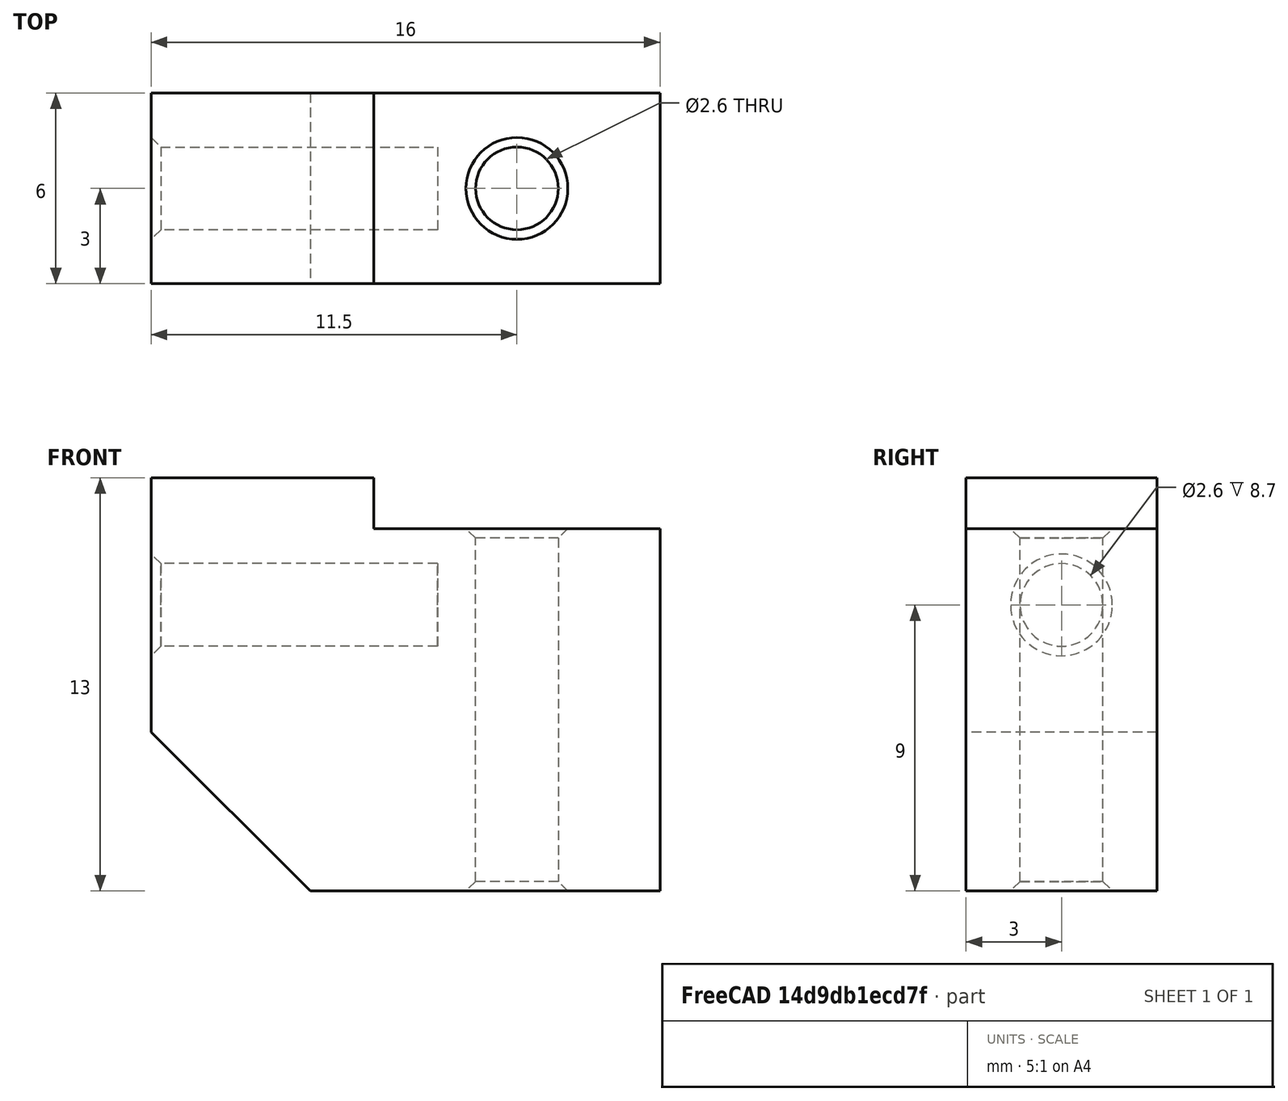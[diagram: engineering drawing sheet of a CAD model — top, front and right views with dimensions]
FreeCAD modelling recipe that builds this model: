
FCSTD DOCUMENT  (FreeCAD 0.21R33675 (Git))
Label: PMB-1
License: All rights reserved
LicenseURL: http://en.wikipedia.org/wiki/All_rights_reserved
objects: TechDraw::DrawViewDimension×9, Sketcher::SketchObject×3, TechDraw::DrawProjGroupItem×3, PartDesign::Pocket×2, PartDesign::Pad×1, PartDesign::Chamfer×1, PartDesign::Body×1, TechDraw::DrawSVGTemplate×1, TechDraw::DrawProjGroup×1, TechDraw::DrawPage×1, Part::Feature×1
note: 27 computed .brp shape members not serialized (recipe doc carries the construction recipe); baked Part::Feature solids carry a one-line shape summary decoded from their .brp

FEATURE [Sketcher::SketchObject] Sketch
  FullyConstrained = true
  MapMode = 5
  Placement = pos=(0,0,0) rot=(1,0,0;1.5708rad)
  Support = -> [XZ_Plane]
  sketch-geometry (7):
    g0: LineSegment StartX=-2e-15 StartY=-2.082e-13 StartZ=0 EndX=7 EndY=-2.082e-13 EndZ=0
    g1: LineSegment StartX=7 StartY=-2.082e-13 StartZ=0 EndX=7 EndY=-1.6 EndZ=0
    g2: LineSegment StartX=7 StartY=-1.6 StartZ=0 EndX=16 EndY=-1.6 EndZ=0
    g3: LineSegment StartX=16 StartY=-1.6 StartZ=0 EndX=16 EndY=-13 EndZ=0
    g4: LineSegment StartX=16 StartY=-13 StartZ=0 EndX=5 EndY=-13 EndZ=0
    g5: LineSegment StartX=5 StartY=-13 StartZ=0 EndX=-2e-15 EndY=-8 EndZ=0
    g6: LineSegment StartX=-2e-15 StartY=-8 StartZ=0 EndX=-2e-15 EndY=-2.078e-13 EndZ=0
  constraints (20):
    c: Horizontal(g0)
    c: Coincident(g0,g1)
    c: Vertical(g1)
    c: Coincident(g1,g2)
    c: Horizontal(g2)
    c: Coincident(g2,g3)
    c: Vertical(g3)
    c: Coincident(g3,g4)
    c: Horizontal(g4)
    c: Coincident(g4,g5)
    c: Coincident(g5,g6)
    c: Coincident(g6,g0)
    c: Coincident(g0,g-1)
    c: Vertical(g6)
    c: DistanceX(g2) = 16
    c: DistanceX(g1,g2) = 9
    c: DistanceY(g1,g1) = 1.6
    c: DistanceY(g4,g0) = 13
    c: Angle(g4,g5) = 2.35619
    c: DistanceX(g5,g4) = 5
FEATURE [PartDesign::Pad] Pad
  Direction = (0,-1,2e-16)
  Length = 6
  Length2 = 10
  Midplane = true
  Placement = pos=(0,0,0) rot=(1,0,0;1.5708rad)
  Profile = -> Sketch
  ReferenceAxis = -> Sketch [N_Axis]
  Type = 0
FEATURE [Sketcher::SketchObject] Sketch001
  FullyConstrained = true
  MapMode = 5
  Support = -> [XY_Plane]
  sketch-geometry (1):
    g0: Circle CenterX=11.5 CenterY=0 CenterZ=0 NormalX=0 NormalY=0 NormalZ=1 AngleXU=0 Radius=1.3
  constraints (3):
    c: PointOnObject(g0,g-1)
    c: DistanceX(g-1,g0) = 11.5
    c: Diameter(g0) = 2.6
FEATURE [PartDesign::Pocket] Pocket
  BaseFeature = -> Pad
  Direction = (0,0,-1)
  Length = 5
  Length2 = 5
  Placement = pos=(0,0,0) rot=(1,0,0;1.5708rad)
  Profile = -> Sketch001
  ReferenceAxis = -> Sketch001 [N_Axis]
  Type = 1
FEATURE [Sketcher::SketchObject] Sketch002
  FullyConstrained = true
  MapMode = 5
  Placement = pos=(0,0,0) rot=(0.57735,0.57735,0.57735;2.0944rad)
  Support = -> [YZ_Plane]
  sketch-geometry (1):
    g0: Circle CenterX=5.7234e-12 CenterY=-4 CenterZ=0 NormalX=0 NormalY=0 NormalZ=1 AngleXU=0 Radius=1.3
  constraints (3):
    c: Vertical(g0,g-1)
    c: DistanceY(g0,g-1) = 4
    c: Diameter(g0) = 2.6
FEATURE [PartDesign::Pocket] Pocket001
  BaseFeature = -> Pocket
  Direction = (-1,2e-16,-3e-16)
  Length = 9
  Length2 = 5
  Placement = pos=(0,0,0) rot=(1,0,0;1.5708rad)
  Profile = -> Sketch002
  ReferenceAxis = -> Sketch002 [N_Axis]
  Reversed = true
  Type = 0
FEATURE [PartDesign::Chamfer] Chamfer
  Angle = 45
  Base = -> Pocket001 [Edge24,Edge26,Edge8]
  BaseFeature = -> Pocket001
  ChamferType = 0
  FlipDirection = false
  Placement = pos=(0,0,0) rot=(1,0,0;1.5708rad)
  Size = 0.3
  Size2 = 1
  SupportTransform = false
  UseAllEdges = false
FEATURE [PartDesign::Body] Body
  Group = -> [Sketch,Pad,Sketch001,Pocket,Sketch002,Pocket001,Chamfer]
  Origin = -> Origin
  Tip = -> Chamfer
FEATURE [TechDraw::DrawSVGTemplate] Template
  EditableTexts = Designed_by_Name=Designed by Name; Drawing_number=Drawing number; FC-Date=Date; FC-SC=Scale; FC-SH=Sheet; FC-Title=Title; Subtitle=Subtitle; Weight=Weight
  Height = 210
  Orientation = 1
  Template = /Applications/FreeCAD-0.21-arm64.app/Contents/Resources/share/Mod/TechDraw/Templates/A4_LandscapeTD.svg
  Width = 297
FEATURE [TechDraw::DrawProjGroupItem] ProjItem  label="Front"
  CoarseView = false
  Direction = (0,-1,0)
  Focus = 100
  HardHidden = false
  IsoCount = 0
  IsoHidden = false
  IsoVisible = true
  LockPosition = true
  Perspective = false
  Rotation = 0
  RotationVector = (1,0,0)
  Scale = 3
  ScaleType = 2
  ScrubCount = 0
  SeamHidden = false
  SeamVisible = false
  SmoothHidden = false
  SmoothVisible = true
  Source = -> [Chamfer]
  Type = 0
  X = 0
  XDirection = (1,0,0)
  Y = 0
FEATURE [TechDraw::DrawProjGroupItem] ProjItem001  label="Top"
  CoarseView = false
  Direction = (0,0,1)
  Focus = 100
  HardHidden = false
  IsoCount = 0
  IsoHidden = false
  IsoVisible = false
  LockPosition = false
  Perspective = false
  Rotation = 0
  RotationVector = (1,0,0)
  ScaleType = 2
  ScrubCount = 0
  SeamHidden = false
  SeamVisible = false
  SmoothHidden = false
  SmoothVisible = true
  Source = -> [Chamfer]
  Type = 4
  X = 0
  XDirection = (1,0,0)
  Y = 53.5
FEATURE [TechDraw::DrawViewDimension] Dimension002
  AngleOverride = false
  Arbitrary = false
  ArbitraryTolerances = false
  EqualTolerance = true
  ExtensionAngle = 0
  FormatSpec = %.2w
  FormatSpecOverTolerance = %+.2w
  FormatSpecUnderTolerance = %+.2w
  Inverted = false
  LineAngle = 0
  LockPosition = false
  MeasureType = 1
  OverTolerance = 0
  References2D = -> [ProjItem001]
  Rotation = 0
  ScaleType = 0
  TheoreticalExact = false
  Type = 1
  UnderTolerance = 0
  X = 8.70547
  Y = -13.6781
FEATURE [TechDraw::DrawViewDimension] Dimension003
  AngleOverride = false
  Arbitrary = false
  ArbitraryTolerances = false
  EqualTolerance = true
  ExtensionAngle = 0
  FormatSpec = ⌀%.2w
  FormatSpecOverTolerance = %+.2w
  FormatSpecUnderTolerance = %+.2w
  Inverted = false
  LineAngle = 0
  LockPosition = false
  MeasureType = 1
  OverTolerance = 0
  References2D = -> [ProjItem001]
  Rotation = 0
  ScaleType = 0
  TheoreticalExact = false
  Type = 5
  UnderTolerance = 0
  X = 31.5596
  Y = -1.45438
FEATURE [TechDraw::DrawViewDimension] Dimension006
  AngleOverride = false
  Arbitrary = false
  ArbitraryTolerances = false
  EqualTolerance = true
  ExtensionAngle = 0
  FormatSpec = %.2w
  FormatSpecOverTolerance = %+.2w
  FormatSpecUnderTolerance = %+.2w
  Inverted = false
  LineAngle = 0
  LockPosition = false
  MeasureType = 1
  OverTolerance = 0
  References2D = -> [ProjItem]
  Rotation = 0
  ScaleType = 0
  TheoreticalExact = false
  Type = 2
  UnderTolerance = 0
  X = -37.5658
  Y = 2.21208
FEATURE [TechDraw::DrawViewDimension] Dimension
  AngleOverride = false
  Arbitrary = false
  ArbitraryTolerances = false
  EqualTolerance = true
  ExtensionAngle = 0
  FormatSpec = %.2w
  FormatSpecOverTolerance = %+.2w
  FormatSpecUnderTolerance = %+.2w
  Inverted = false
  LineAngle = 0
  LockPosition = false
  MeasureType = 1
  OverTolerance = 0
  References2D = -> [ProjItem]
  Rotation = 0
  ScaleType = 0
  TheoreticalExact = false
  Type = 1
  UnderTolerance = 0
  X = -1.45161
  Y = 34.5854
FEATURE [TechDraw::DrawViewDimension] Dimension001
  AngleOverride = false
  Arbitrary = false
  ArbitraryTolerances = false
  EqualTolerance = true
  ExtensionAngle = 0
  FormatSpec = %.2w
  FormatSpecOverTolerance = %+.2w
  FormatSpecUnderTolerance = %+.2w
  Inverted = false
  LineAngle = 0
  LockPosition = false
  MeasureType = 1
  OverTolerance = 0
  References2D = -> [ProjItem001]
  Rotation = 0
  ScaleType = 0
  TheoreticalExact = false
  Type = 1
  UnderTolerance = 0
  X = 0.316812
  Y = 26.6328
FEATURE [TechDraw::DrawViewDimension] Dimension008
  AngleOverride = false
  Arbitrary = false
  ArbitraryTolerances = false
  EqualTolerance = true
  ExtensionAngle = 0
  FormatSpec = %.2w
  FormatSpecOverTolerance = %+.2w
  FormatSpecUnderTolerance = %+.2w
  Inverted = false
  LineAngle = 0
  LockPosition = false
  MeasureType = 1
  OverTolerance = 0
  References2D = -> [ProjItem]
  Rotation = 0
  ScaleType = 0
  TheoreticalExact = false
  Type = 2
  UnderTolerance = 0
  X = 28.8658
  Y = 3.10476
FEATURE [TechDraw::DrawProjGroupItem] ProjItem002  label="Left"
  CoarseView = false
  Direction = (-1,-1e-16,0)
  Focus = 100
  HardHidden = false
  IsoCount = 0
  IsoHidden = false
  IsoVisible = false
  LockPosition = false
  Perspective = false
  Rotation = 0
  RotationVector = (1,0,0)
  ScaleType = 2
  ScrubCount = 0
  SeamHidden = false
  SeamVisible = false
  SmoothHidden = false
  SmoothVisible = true
  Source = -> [Chamfer]
  Type = 1
  X = -58
  XDirection = (1e-16,-1,0)
  Y = 0
FEATURE [TechDraw::DrawProjGroup] ProjGroup
  Anchor = -> ProjItem
  AutoDistribute = true
  LockPosition = false
  ProjectionType = 1
  Rotation = 0
  Scale = 3
  ScaleType = 2
  Source = -> [Chamfer]
  Views = -> [ProjItem,ProjItem001,ProjItem002]
  X = 166.847
  Y = 107.168
  spacingX = 25
  spacingY = 25
FEATURE [TechDraw::DrawViewDimension] Dimension004
  AngleOverride = false
  Arbitrary = false
  ArbitraryTolerances = false
  EqualTolerance = true
  ExtensionAngle = 0
  FormatSpec = ⌀%.2w
  FormatSpecOverTolerance = %+.2w
  FormatSpecUnderTolerance = %+.2w
  Inverted = false
  LineAngle = 0
  LockPosition = false
  MeasureType = 1
  OverTolerance = 0
  References2D = -> [ProjItem002]
  Rotation = 0
  ScaleType = 0
  TheoreticalExact = false
  Type = 5
  UnderTolerance = 0
  X = -22.1653
  Y = -0.510507
FEATURE [TechDraw::DrawViewDimension] Dimension005
  AngleOverride = false
  Arbitrary = false
  ArbitraryTolerances = false
  EqualTolerance = true
  ExtensionAngle = 0
  FormatSpec = %.2w
  FormatSpecOverTolerance = %+.2w
  FormatSpecUnderTolerance = %+.2w
  Inverted = false
  LineAngle = 0
  LockPosition = false
  MeasureType = 1
  OverTolerance = 0
  References2D = -> [ProjItem002]
  Rotation = 0
  ScaleType = 0
  TheoreticalExact = false
  Type = 2
  UnderTolerance = 0
  X = -24.3538
  Y = 17.1135
FEATURE [TechDraw::DrawViewDimension] Dimension007
  AngleOverride = false
  Arbitrary = false
  ArbitraryTolerances = false
  EqualTolerance = true
  ExtensionAngle = 0
  FormatSpec = %.2w
  FormatSpecOverTolerance = %+.2w
  FormatSpecUnderTolerance = %+.2w
  Inverted = false
  LineAngle = 0
  LockPosition = false
  MeasureType = 1
  OverTolerance = 0
  References2D = -> [ProjItem002]
  Rotation = 0
  ScaleType = 0
  TheoreticalExact = false
  Type = 1
  UnderTolerance = 0
  X = -1.87446
  Y = 36.2459
FEATURE [TechDraw::DrawPage] Page
  KeepUpdated = true
  NextBalloonIndex = 1
  ProjectionType = 0
  Template = -> Template
  Views = -> [ProjGroup,Dimension,Dimension001,Dimension002,Dimension003,Dimension004,Dimension005,Dimension006,Dimension007,Dimension008]
FEATURE [Part::Feature] Chamfer001  label="PMB-1"
  Placement = pos=(0,0,0) rot=(1,0,0;1.5708rad)
  shape: bbox 16 x 6 x 13 mm, 15 faces (baked)
